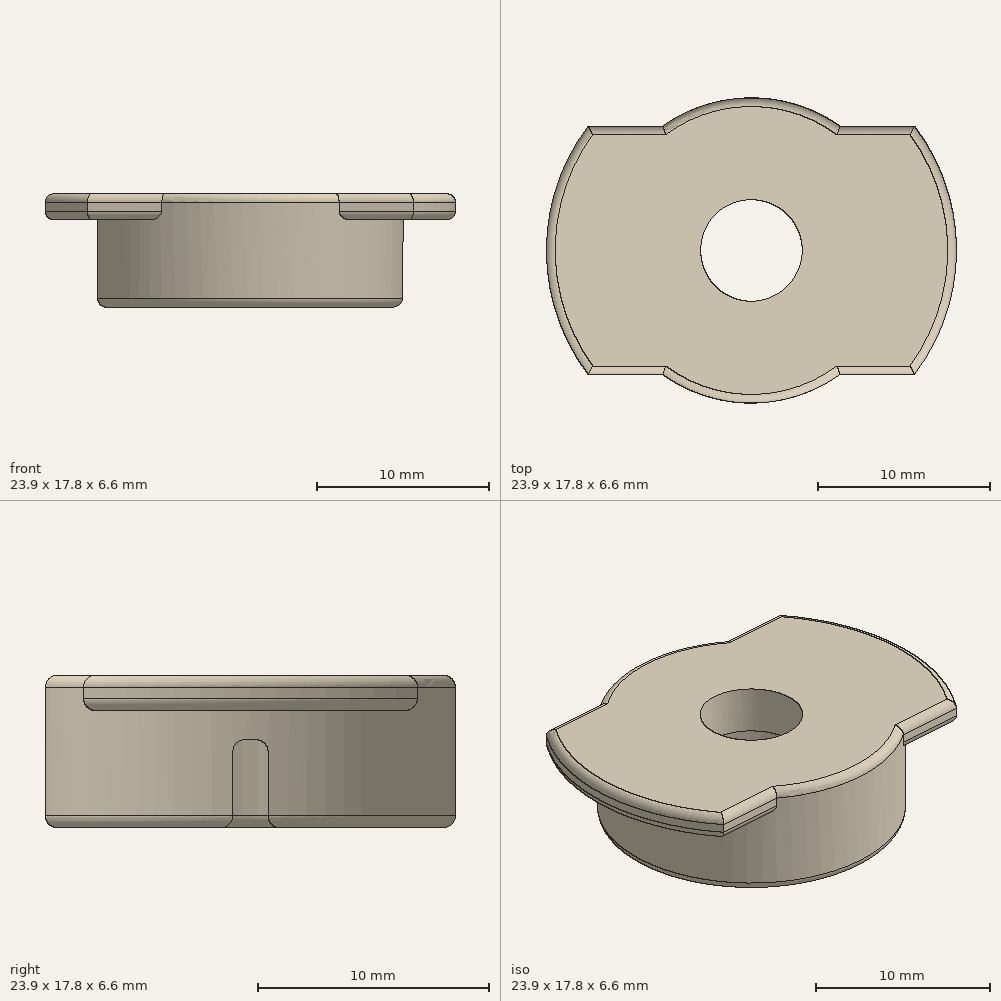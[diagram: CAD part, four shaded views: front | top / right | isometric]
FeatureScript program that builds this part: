
annotation { "Feature Type Name" : "Feature", "Feature Type Description" : "" }
export const myFeature = defineFeature(function(context is Context, id is Id, definition is map)
    precondition{}
    {
        {
            var Q0;
            Q0=qCreatedBy(makeId("Top.planeOp"),FACE);
            var sketch = newSketch(context, id + "F0", { "sketchPlane" : qUnion([Q0])});
            skCircle(sketch, "E0", {"center": v(0, 0) * mm, "radius": 11.94 * mm});
            skSolve(sketch);
        }
        {
            var Q0;
            Q0=makeQuery(id+"F0.imprint","IMPRINT",FACE,{"disambiguationData":[TD([[makeQuery(id+"F0.imprint","IMPRINT",EDGE,{"derivedFrom":sQuery(id+"F0.wireOp",EDGE,"E0")}),1.0]])]});
            var sketch = newSketch(context, id + "F1", { "sketchPlane" : qUnion([Q0])});
            skLineSegment(sketch, "E1", {"start": v(9.5, 7.24) * mm, "end": v(-9.5, 7.24) * mm});
            skLineSegment(sketch, "E2", {"start": v(9.5, -7.24) * mm, "end": v(-9.5, -7.24) * mm});
            skLineSegment(sketch, "E3", {"start": v(-9.5, 7.24) * mm, "end": v(-9.5, -7.24) * mm, "construction": true});
            skLineSegment(sketch, "E4", {"start": v(9.5, 7.24) * mm, "end": v(9.5, -7.24) * mm, "construction": true});
            skSolve(sketch);
        }
        {
            var Q0;
            Q0=qSketchRegion(id+"F0",true);
            extrude(context, id + "F2", {"entities" : qUnion([Q0]), "depth" : 1.52 * mm, "offsetDistance" : 25.4 * mm});
        }
        {
            var Q0;
            {var subQ0=sQuery(id+"F1.wireOp",EDGE,"E1");Q0=makeQuery(id+"F1.imprint","IMPRINT",FACE,{"disambiguationData":[TD([[makeQuery(id+"F1.imprint","IMPRINT",EDGE,{"derivedFrom":subQ0}),-1.0]])]});}
            var Q1;
            {var subQ0=sQuery(id+"F1.wireOp",EDGE,"E2");Q1=makeQuery(id+"F1.imprint","IMPRINT",FACE,{"disambiguationData":[TD([[makeQuery(id+"F1.imprint","IMPRINT",EDGE,{"derivedFrom":subQ0}),1.0]])]});}
            extrude(context, id + "F3", {"entities" : qUnion([Q0, Q1]), "operationType" : NewBodyOperationType.REMOVE, "depth" : 2.54 * mm, "offsetDistance" : 25.4 * mm, "hasSecondDirection" : true, "secondDirectionOppositeDirection" : true, "secondDirectionDepth" : 25.4 * mm});
        }
        {
            var Q0;
            Q0=makeQuery(id+"F2.opExtrude","CAP_FACE",FACE,{"disambiguationData":[OSD([sQuery(id+"F0.wireOp",EDGE,"E0")])],"isStart":true});
            var sketch = newSketch(context, id + "F4", { "sketchPlane" : qUnion([Q0])});
            skCircle(sketch, "E5", {"center": v(0, 0) * mm, "radius": 8.9 * mm});
            skSolve(sketch);
        }
        {
            var Q0;
            Q0=qSketchRegion(id+"F4",true);
            extrude(context, id + "F5", {"entities" : qUnion([Q0]), "operationType" : NewBodyOperationType.ADD, "oppositeDirection" : true, "depth" : 1.52 * mm, "offsetDistance" : 25.4 * mm});
        }
        {
            var Q0;
            Q0=makeQuery(id+"F5.boolean.opBoolean","MERGE",FACE,{"derivedFrom":[makeQuery(id+"F2.opExtrude","CAP_FACE",FACE,{"disambiguationData":[OSD([sQuery(id+"F0.wireOp",EDGE,"E0")])],"isStart":true}),makeQuery(id+"F5.opExtrude","CAP_FACE",FACE,{"disambiguationData":[OSD([sQuery(id+"F4.wireOp",EDGE,"E5")])],"isStart":true})]});
            var sketch = newSketch(context, id + "F6", { "sketchPlane" : qUnion([Q0])});
            skCircle(sketch, "E6", {"center": v(0, 0) * mm, "radius": 8.9 * mm});
            skSolve(sketch);
        }
        {
            var Q0;
            Q0=qSketchRegion(id+"F6",true);
            extrude(context, id + "F7", {"entities" : qUnion([Q0]), "operationType" : NewBodyOperationType.ADD, "depth" : 5.08 * mm, "offsetDistance" : 25.4 * mm});
        }
        {
            var Q0;
            Q0=makeQuery(id+"F7.opExtrude","CAP_FACE",FACE,{"disambiguationData":[OSD([sQuery(id+"F6.wireOp",EDGE,"E6")])],"isStart":false});
            var sketch = newSketch(context, id + "F8", { "sketchPlane" : qUnion([Q0])});
            skCircle(sketch, "E7", {"center": v(0, 0) * mm, "radius": 7.37 * mm});
            skSolve(sketch);
        }
        {
            var Q0;
            Q0 = qSketchRegion(id + "F8", true);
            extrude(context, id + "F9", {"entities" : qUnion([Q0]), "operationType" : NewBodyOperationType.REMOVE, "oppositeDirection" : true, "depth" : 5.08 * mm, "offsetDistance" : 25.4 * mm});
        }
        {
            var Q0;
            Q0=makeQuery(id+"F7.opExtrude","CAP_FACE",FACE,{"disambiguationData":[OSD([sQuery(id+"F6.wireOp",EDGE,"E6")])],"isStart":false});
            var sketch = newSketch(context, id + "F10", { "sketchPlane" : qUnion([Q0])});
            skLineSegment(sketch, "E8", {"start": v(8.86, -0.76) * mm, "end": v(7.33, -0.76) * mm});
            skLineSegment(sketch, "E9", {"start": v(8.86, 0.76) * mm, "end": v(7.33, 0.76) * mm});
            skLineSegment(sketch, "E10", {"start": v(0, 0) * mm, "end": v(8.9, 0) * mm, "construction": true});
            skArc(sketch, "E11", {"start": v(8.86, -0.76) * mm, "mid": v(8.9, 0) * mm, "end": v(8.86, 0.76) * mm});
            skArc(sketch, "E12", {"start": v(7.33, -0.76) * mm, "mid": v(7.37, 0) * mm, "end": v(7.33, 0.76) * mm});
            skSolve(sketch);
        }
        {
            var Q0;
            Q0=qCreatedBy(makeId("Front.planeOp"),FACE);
            var sketch = newSketch(context, id + "F11", { "sketchPlane" : qUnion([Q0])});
            skLineSegment(sketch, "E13", {"start": v(0, 0) * mm, "end": v(0, -7.62) * mm, "construction": true});
            skSolve(sketch);
        }
        {
            var Q0;
            Q0=makeQuery(id+"F10.imprint","IMPRINT",FACE,{"disambiguationData":[TD([[makeQuery(id+"F10.imprint","IMPRINT",EDGE,{"derivedFrom":sQuery(id+"F10.wireOp",EDGE,"E8")}),-1.0]])]});
            var Q1;
            Q1=makeQuery(id+"FOOJxRczT3KKHVt_1.3.F10.imprint","IMPRINT",FACE,{"disambiguationData":[TD([[makeQuery(id+"FOOJxRczT3KKHVt_1.3.F10.imprint","IMPRINT",EDGE,{"derivedFrom":sQuery(id+"FOOJxRczT3KKHVt_1.3.F10.wireOp",EDGE,"E8")}),-1.0]])]});
            var Q2;
            Q2=makeQuery(id+"FOOJxRczT3KKHVt_1.2.F10.imprint","IMPRINT",FACE,{"disambiguationData":[TD([[makeQuery(id+"FOOJxRczT3KKHVt_1.2.F10.imprint","IMPRINT",EDGE,{"derivedFrom":sQuery(id+"FOOJxRczT3KKHVt_1.2.F10.wireOp",EDGE,"E8")}),-1.0]])]});
            var Q3;
            Q3=makeQuery(id+"FOOJxRczT3KKHVt_1.1.F10.imprint","IMPRINT",FACE,{"disambiguationData":[TD([[makeQuery(id+"FOOJxRczT3KKHVt_1.1.F10.imprint","IMPRINT",EDGE,{"derivedFrom":sQuery(id+"FOOJxRczT3KKHVt_1.1.F10.wireOp",EDGE,"E8")}),-1.0]])]});
            extrude(context, id + "F12", {"entities" : qUnion([Q0, Q1, Q2, Q3]), "operationType" : NewBodyOperationType.REMOVE, "oppositeDirection" : true, "depth" : 3.8 * mm, "offsetDistance" : 25.4 * mm});
        }
        {
            var Q0;
            Q0=makeQuery(id+"F12.boolean.opBoolean","COPY",EDGE,{"derivedFrom":makeQuery(id+"F12.opExtrude","CAP_EDGE",EDGE,{"disambiguationData":[OSD([sQuery(id+"FOOJxRczT3KKHVt_1.2.F10.wireOp",EDGE,"E9")])],"isStart":false})});
            var Q1;
            Q1=makeQuery(id+"F12.boolean.opBoolean","COPY",EDGE,{"derivedFrom":makeQuery(id+"F12.opExtrude","CAP_EDGE",EDGE,{"disambiguationData":[OSD([sQuery(id+"FOOJxRczT3KKHVt_1.2.F10.wireOp",EDGE,"E8")])],"isStart":false})});
            var Q2;
            Q2=makeQuery(id+"F12.boolean.opBoolean","COPY",EDGE,{"derivedFrom":makeQuery(id+"F12.opExtrude","CAP_EDGE",EDGE,{"disambiguationData":[OSD([sQuery(id+"FOOJxRczT3KKHVt_1.1.F10.wireOp",EDGE,"E9")])],"isStart":false})});
            var Q3;
            Q3=makeQuery(id+"F12.boolean.opBoolean","COPY",EDGE,{"derivedFrom":makeQuery(id+"F12.opExtrude","CAP_EDGE",EDGE,{"disambiguationData":[OSD([sQuery(id+"FOOJxRczT3KKHVt_1.3.F10.wireOp",EDGE,"E8")])],"isStart":false})});
            var Q4;
            Q4=makeQuery(id+"F12.boolean.opBoolean","COPY",EDGE,{"derivedFrom":makeQuery(id+"F12.opExtrude","CAP_EDGE",EDGE,{"disambiguationData":[OSD([sQuery(id+"F10.wireOp",EDGE,"E9")])],"isStart":false})});
            var Q5;
            Q5=makeQuery(id+"F12.boolean.opBoolean","COPY",EDGE,{"derivedFrom":makeQuery(id+"F12.opExtrude","CAP_EDGE",EDGE,{"disambiguationData":[OSD([sQuery(id+"FOOJxRczT3KKHVt_1.3.F10.wireOp",EDGE,"E9")])],"isStart":false})});
            var Q6;
            Q6=makeQuery(id+"F12.boolean.opBoolean","COPY",EDGE,{"derivedFrom":makeQuery(id+"F12.opExtrude","CAP_EDGE",EDGE,{"disambiguationData":[OSD([sQuery(id+"F10.wireOp",EDGE,"E8")])],"isStart":false})});
            var Q7;
            Q7=makeQuery(id+"F12.boolean.opBoolean","COPY",EDGE,{"derivedFrom":makeQuery(id+"F12.opExtrude","CAP_EDGE",EDGE,{"disambiguationData":[OSD([sQuery(id+"FOOJxRczT3KKHVt_1.1.F10.wireOp",EDGE,"E8")])],"isStart":false})});
            fillet(context, id + "F13", {"entities" : qUnion([Q0, Q1, Q2, Q3, Q4, Q5, Q6, Q7]), "radius" : 0.5 * mm, "tangentPropagation" : true, "allowEdgeOverflow" : false});
        }
        {
            var Q0;
            Q0=makeQuery(id+"F12.boolean.opBoolean","COPY",EDGE,{"derivedFrom":makeQuery(id+"F12.opExtrude","SWEPT_EDGE",EDGE,{"disambiguationData":[OSD([sQuery(id+"F6.wireOp",EDGE,"E6"),sQuery(id+"F10.wireOp",EDGE,"E8"),sQuery(id+"F10.wireOp",EDGE,"E11")])]})});
            var Q1;
            Q1=makeQuery(id+"F12.boolean.opBoolean","COPY",EDGE,{"derivedFrom":makeQuery(id+"F12.opExtrude","SWEPT_EDGE",EDGE,{"disambiguationData":[OSD([sQuery(id+"F6.wireOp",EDGE,"E6"),sQuery(id+"F10.wireOp",EDGE,"E9"),sQuery(id+"F10.wireOp",EDGE,"E11")])]})});
            var Q2;
            Q2=makeQuery(id+"F12.boolean.opBoolean","COPY",EDGE,{"derivedFrom":makeQuery(id+"F12.opExtrude","SWEPT_EDGE",EDGE,{"disambiguationData":[OSD([sQuery(id+"F8.wireOp",EDGE,"E7"),sQuery(id+"F10.wireOp",EDGE,"E8"),sQuery(id+"F10.wireOp",EDGE,"E12")])]})});
            var Q3;
            Q3=makeQuery(id+"F12.boolean.opBoolean","COPY",EDGE,{"derivedFrom":makeQuery(id+"F12.opExtrude","SWEPT_EDGE",EDGE,{"disambiguationData":[OSD([sQuery(id+"F8.wireOp",EDGE,"E7"),sQuery(id+"F10.wireOp",EDGE,"E9"),sQuery(id+"F10.wireOp",EDGE,"E12")])]})});
            var Q4;
            {var subQ0=sQuery(id+"F6.wireOp",EDGE,"E6");Q4=makeQuery(id+"F12.boolean.opBoolean","SPLIT",EDGE,{"disambiguationData":[TD([makeQuery(id+"F12.opExtrude","SWEPT_FACE",FACE,{"disambiguationData":[OSD([sQuery(id+"F10.wireOp",EDGE,"E8")])]})])],"derivedFrom":makeQuery(id+"F7.opExtrude","CAP_EDGE",EDGE,{"disambiguationData":[OSD([subQ0])],"isStart":false})});}
            var Q5;
            {var subQ0=sQuery(id+"F8.wireOp",EDGE,"E7");Q5=makeQuery(id+"F12.boolean.opBoolean","SPLIT",EDGE,{"disambiguationData":[TD([makeQuery(id+"F12.opExtrude","SWEPT_FACE",FACE,{"disambiguationData":[OSD([sQuery(id+"F10.wireOp",EDGE,"E8")])]})])],"derivedFrom":makeQuery(id+"F9.boolean.opBoolean","COPY",EDGE,{"derivedFrom":makeQuery(id+"F9.opExtrude","CAP_EDGE",EDGE,{"disambiguationData":[OSD([subQ0])],"isStart":true})})});}
            var Q6;
            {var subQ0=sQuery(id+"F6.wireOp",EDGE,"E6");Q6=makeQuery(id+"F12.boolean.opBoolean","SPLIT",EDGE,{"disambiguationData":[TD([makeQuery(id+"F12.opExtrude","SWEPT_FACE",FACE,{"disambiguationData":[OSD([sQuery(id+"F10.wireOp",EDGE,"E9")])]})])],"derivedFrom":makeQuery(id+"F7.opExtrude","CAP_EDGE",EDGE,{"disambiguationData":[OSD([subQ0])],"isStart":false})});}
            var Q7;
            {var subQ0=sQuery(id+"F8.wireOp",EDGE,"E7");Q7=makeQuery(id+"F12.boolean.opBoolean","SPLIT",EDGE,{"disambiguationData":[TD([makeQuery(id+"F12.opExtrude","SWEPT_FACE",FACE,{"disambiguationData":[OSD([sQuery(id+"F10.wireOp",EDGE,"E9")])]})])],"derivedFrom":makeQuery(id+"F9.boolean.opBoolean","COPY",EDGE,{"derivedFrom":makeQuery(id+"F9.opExtrude","CAP_EDGE",EDGE,{"disambiguationData":[OSD([subQ0])],"isStart":true})})});}
            var Q8;
            Q8=makeQuery(id+"F12.boolean.opBoolean","COPY",EDGE,{"derivedFrom":makeQuery(id+"F12.opExtrude","CAP_EDGE",EDGE,{"disambiguationData":[OSD([sQuery(id+"F10.wireOp",EDGE,"E9")])],"isStart":true})});
            var Q9;
            Q9=makeQuery(id+"F12.boolean.opBoolean","COPY",EDGE,{"derivedFrom":makeQuery(id+"F12.opExtrude","CAP_EDGE",EDGE,{"disambiguationData":[OSD([sQuery(id+"F10.wireOp",EDGE,"E8")])],"isStart":true})});
            var Q10;
            {var subQ0=sQuery(id+"F6.wireOp",EDGE,"E6");Q10=makeQuery(id+"F12.boolean.opBoolean","SPLIT",EDGE,{"disambiguationData":[TD([makeQuery(id+"F12.opExtrude","SWEPT_FACE",FACE,{"disambiguationData":[OSD([sQuery(id+"FOOJxRczT3KKHVt_1.2.F10.wireOp",EDGE,"E9")])]})])],"derivedFrom":makeQuery(id+"F7.opExtrude","CAP_EDGE",EDGE,{"disambiguationData":[OSD([subQ0])],"isStart":false})});}
            var Q11;
            {var subQ0=sQuery(id+"F8.wireOp",EDGE,"E7");Q11=makeQuery(id+"F12.boolean.opBoolean","SPLIT",EDGE,{"disambiguationData":[TD([makeQuery(id+"F12.opExtrude","SWEPT_FACE",FACE,{"disambiguationData":[OSD([sQuery(id+"FOOJxRczT3KKHVt_1.2.F10.wireOp",EDGE,"E9")])]})])],"derivedFrom":makeQuery(id+"F9.boolean.opBoolean","COPY",EDGE,{"derivedFrom":makeQuery(id+"F9.opExtrude","CAP_EDGE",EDGE,{"disambiguationData":[OSD([subQ0])],"isStart":true})})});}
            var Q12;
            Q12=makeQuery(id+"F12.boolean.opBoolean","COPY",EDGE,{"derivedFrom":makeQuery(id+"F12.opExtrude","CAP_EDGE",EDGE,{"disambiguationData":[OSD([sQuery(id+"FOOJxRczT3KKHVt_1.3.F10.wireOp",EDGE,"E8")])],"isStart":true})});
            var Q13;
            Q13=makeQuery(id+"F12.boolean.opBoolean","COPY",EDGE,{"derivedFrom":makeQuery(id+"F12.opExtrude","CAP_EDGE",EDGE,{"disambiguationData":[OSD([sQuery(id+"FOOJxRczT3KKHVt_1.3.F10.wireOp",EDGE,"E9")])],"isStart":true})});
            var Q14;
            Q14=makeQuery(id+"F12.boolean.opBoolean","COPY",EDGE,{"derivedFrom":makeQuery(id+"F12.opExtrude","SWEPT_EDGE",EDGE,{"disambiguationData":[OSD([sQuery(id+"FOOJxRczT3KKHVt_1.3.F10.wireOp",EDGE,"E8"),sQuery(id+"FOOJxRczT3KKHVt_1.3.F10.wireOp",EDGE,"E11")])]})});
            var Q15;
            Q15=makeQuery(id+"F12.boolean.opBoolean","COPY",EDGE,{"derivedFrom":makeQuery(id+"F12.opExtrude","SWEPT_EDGE",EDGE,{"disambiguationData":[OSD([sQuery(id+"FOOJxRczT3KKHVt_1.3.F10.wireOp",EDGE,"E9"),sQuery(id+"FOOJxRczT3KKHVt_1.3.F10.wireOp",EDGE,"E11")])]})});
            var Q16;
            Q16=makeQuery(id+"F12.boolean.opBoolean","COPY",EDGE,{"derivedFrom":makeQuery(id+"F12.opExtrude","CAP_EDGE",EDGE,{"disambiguationData":[OSD([sQuery(id+"FOOJxRczT3KKHVt_1.1.F10.wireOp",EDGE,"E9")])],"isStart":true})});
            var Q17;
            Q17=makeQuery(id+"F12.boolean.opBoolean","COPY",EDGE,{"derivedFrom":makeQuery(id+"F12.opExtrude","CAP_EDGE",EDGE,{"disambiguationData":[OSD([sQuery(id+"FOOJxRczT3KKHVt_1.1.F10.wireOp",EDGE,"E8")])],"isStart":true})});
            var Q18;
            Q18=makeQuery(id+"F12.boolean.opBoolean","COPY",EDGE,{"derivedFrom":makeQuery(id+"F12.opExtrude","SWEPT_EDGE",EDGE,{"disambiguationData":[OSD([sQuery(id+"FOOJxRczT3KKHVt_1.1.F10.wireOp",EDGE,"E9"),sQuery(id+"FOOJxRczT3KKHVt_1.1.F10.wireOp",EDGE,"E11")])]})});
            var Q19;
            Q19=makeQuery(id+"F12.boolean.opBoolean","COPY",EDGE,{"derivedFrom":makeQuery(id+"F12.opExtrude","CAP_EDGE",EDGE,{"disambiguationData":[OSD([sQuery(id+"FOOJxRczT3KKHVt_1.2.F10.wireOp",EDGE,"E9")])],"isStart":true})});
            var Q20;
            Q20=makeQuery(id+"F12.boolean.opBoolean","COPY",EDGE,{"derivedFrom":makeQuery(id+"F12.opExtrude","CAP_EDGE",EDGE,{"disambiguationData":[OSD([sQuery(id+"FOOJxRczT3KKHVt_1.2.F10.wireOp",EDGE,"E8")])],"isStart":true})});
            var Q21;
            {var subQ0=sQuery(id+"F8.wireOp",EDGE,"E7");Q21=makeQuery(id+"F12.boolean.opBoolean","SPLIT",EDGE,{"disambiguationData":[TD([makeQuery(id+"F12.opExtrude","SWEPT_FACE",FACE,{"disambiguationData":[OSD([sQuery(id+"FOOJxRczT3KKHVt_1.1.F10.wireOp",EDGE,"E9")])]})])],"derivedFrom":makeQuery(id+"F9.boolean.opBoolean","COPY",EDGE,{"derivedFrom":makeQuery(id+"F9.opExtrude","CAP_EDGE",EDGE,{"disambiguationData":[OSD([subQ0])],"isStart":true})})});}
            var Q22;
            {var subQ0=sQuery(id+"F6.wireOp",EDGE,"E6");Q22=makeQuery(id+"F12.boolean.opBoolean","SPLIT",EDGE,{"disambiguationData":[TD([makeQuery(id+"F12.opExtrude","SWEPT_FACE",FACE,{"disambiguationData":[OSD([sQuery(id+"FOOJxRczT3KKHVt_1.1.F10.wireOp",EDGE,"E9")])]})])],"derivedFrom":makeQuery(id+"F7.opExtrude","CAP_EDGE",EDGE,{"disambiguationData":[OSD([subQ0])],"isStart":false})});}
            var Q23;
            {var subQ0=sQuery(id+"F6.wireOp",EDGE,"E6");Q23=makeQuery(id+"F12.boolean.opBoolean","SPLIT",FACE,{"disambiguationData":[TD([makeQuery(id+"F12.opExtrude","SWEPT_FACE",FACE,{"disambiguationData":[OSD([sQuery(id+"FOOJxRczT3KKHVt_1.1.F10.wireOp",EDGE,"E9")])]})])],"derivedFrom":makeQuery(id+"F7.opExtrude","CAP_FACE",FACE,{"disambiguationData":[OSD([subQ0])],"isStart":false})});}
            var Q24;
            Q24=makeQuery(id+"F12.boolean.opBoolean","COPY",EDGE,{"derivedFrom":makeQuery(id+"F12.opExtrude","SWEPT_EDGE",EDGE,{"disambiguationData":[OSD([sQuery(id+"FOOJxRczT3KKHVt_1.2.F10.wireOp",EDGE,"E8"),sQuery(id+"FOOJxRczT3KKHVt_1.2.F10.wireOp",EDGE,"E11")])]})});
            var Q25;
            Q25=makeQuery(id+"F12.boolean.opBoolean","COPY",EDGE,{"derivedFrom":makeQuery(id+"F12.opExtrude","SWEPT_EDGE",EDGE,{"disambiguationData":[OSD([sQuery(id+"FOOJxRczT3KKHVt_1.2.F10.wireOp",EDGE,"E9"),sQuery(id+"FOOJxRczT3KKHVt_1.2.F10.wireOp",EDGE,"E11")])]})});
            var Q26;
            Q26=makeQuery(id+"F12.boolean.opBoolean","COPY",EDGE,{"derivedFrom":makeQuery(id+"F12.opExtrude","SWEPT_EDGE",EDGE,{"disambiguationData":[OSD([sQuery(id+"FOOJxRczT3KKHVt_1.2.F10.wireOp",EDGE,"E9"),sQuery(id+"FOOJxRczT3KKHVt_1.2.F10.wireOp",EDGE,"E12")])]})});
            var Q27;
            Q27=makeQuery(id+"F12.boolean.opBoolean","COPY",EDGE,{"derivedFrom":makeQuery(id+"F12.opExtrude","SWEPT_EDGE",EDGE,{"disambiguationData":[OSD([sQuery(id+"FOOJxRczT3KKHVt_1.2.F10.wireOp",EDGE,"E8"),sQuery(id+"FOOJxRczT3KKHVt_1.2.F10.wireOp",EDGE,"E12")])]})});
            var Q28;
            Q28=makeQuery(id+"F12.boolean.opBoolean","COPY",EDGE,{"derivedFrom":makeQuery(id+"F12.opExtrude","SWEPT_EDGE",EDGE,{"disambiguationData":[OSD([sQuery(id+"FOOJxRczT3KKHVt_1.1.F10.wireOp",EDGE,"E9"),sQuery(id+"FOOJxRczT3KKHVt_1.1.F10.wireOp",EDGE,"E12")])]})});
            var Q29;
            Q29=makeQuery(id+"F12.boolean.opBoolean","COPY",EDGE,{"derivedFrom":makeQuery(id+"F12.opExtrude","SWEPT_EDGE",EDGE,{"disambiguationData":[OSD([sQuery(id+"FOOJxRczT3KKHVt_1.1.F10.wireOp",EDGE,"E8"),sQuery(id+"FOOJxRczT3KKHVt_1.1.F10.wireOp",EDGE,"E12")])]})});
            var Q30;
            Q30=makeQuery(id+"F12.boolean.opBoolean","COPY",EDGE,{"derivedFrom":makeQuery(id+"F12.opExtrude","SWEPT_EDGE",EDGE,{"disambiguationData":[OSD([sQuery(id+"FOOJxRczT3KKHVt_1.3.F10.wireOp",EDGE,"E8"),sQuery(id+"FOOJxRczT3KKHVt_1.3.F10.wireOp",EDGE,"E12")])]})});
            var Q31;
            Q31=makeQuery(id+"F12.boolean.opBoolean","COPY",EDGE,{"derivedFrom":makeQuery(id+"F12.opExtrude","SWEPT_EDGE",EDGE,{"disambiguationData":[OSD([sQuery(id+"FOOJxRczT3KKHVt_1.3.F10.wireOp",EDGE,"E9"),sQuery(id+"FOOJxRczT3KKHVt_1.3.F10.wireOp",EDGE,"E12")])]})});
            fillet(context, id + "F14", {"entities" : qUnion([Q0, Q1, Q2, Q3, Q4, Q5, Q6, Q7, Q8, Q9, Q10, Q11, Q12, Q13, Q14, Q15, Q16, Q17, Q18, Q19, Q20, Q21, Q22, Q23, Q24, Q25, Q26, Q27, Q28, Q29, Q30, Q31]), "radius" : 0.5 * mm, "tangentPropagation" : true, "allowEdgeOverflow" : false});
        }
        {
            var Q0;
            {var subQ0=sQuery(id+"F4.wireOp",EDGE,"E5");Q0=makeQuery(id+"F5.boolean.opBoolean","SPLIT",EDGE,{"disambiguationData":[TD([makeQuery(id+"F3.boolean.opBoolean","COPY",FACE,{"derivedFrom":makeQuery(id+"F3.opExtrude","SWEPT_FACE",FACE,{"disambiguationData":[OSD([sQuery(id+"F1.wireOp",EDGE,"E1")])]})})])],"derivedFrom":makeQuery(id+"F5.opExtrude","CAP_EDGE",EDGE,{"disambiguationData":[OSD([subQ0])],"isStart":false})});}
            var Q1;
            {var subQ0=sQuery(id+"F4.wireOp",EDGE,"E5");Q1=makeQuery(id+"F5.boolean.opBoolean","SPLIT",EDGE,{"disambiguationData":[TD([makeQuery(id+"F3.boolean.opBoolean","COPY",FACE,{"derivedFrom":makeQuery(id+"F3.opExtrude","SWEPT_FACE",FACE,{"disambiguationData":[OSD([sQuery(id+"F1.wireOp",EDGE,"E2")])]})})])],"derivedFrom":makeQuery(id+"F5.opExtrude","CAP_EDGE",EDGE,{"disambiguationData":[OSD([subQ0])],"isStart":false})});}
            var Q2;
            Q2=makeQuery(id+"F5.boolean.opBoolean","SPLIT",EDGE,{"disambiguationData":[OD(0.0)],"derivedFrom":makeQuery(id+"F3.boolean.opBoolean","INTERSECT",EDGE,{"derivedFrom":[makeQuery(id+"F2.opExtrude","CAP_FACE",FACE,{"disambiguationData":[OSD([sQuery(id+"F0.wireOp",EDGE,"E0")])],"isStart":false}),makeQuery(id+"F3.opExtrude","SWEPT_FACE",FACE,{"disambiguationData":[OSD([sQuery(id+"F1.wireOp",EDGE,"E2")])]})]})});
            var Q3;
            Q3=makeQuery(id+"F5.boolean.opBoolean","SPLIT",EDGE,{"disambiguationData":[OD(0.0)],"derivedFrom":makeQuery(id+"F3.boolean.opBoolean","INTERSECT",EDGE,{"derivedFrom":[makeQuery(id+"F2.opExtrude","CAP_FACE",FACE,{"disambiguationData":[OSD([sQuery(id+"F0.wireOp",EDGE,"E0")])],"isStart":false}),makeQuery(id+"F3.opExtrude","SWEPT_FACE",FACE,{"disambiguationData":[OSD([sQuery(id+"F1.wireOp",EDGE,"E1")])]})]})});
            var Q4;
            Q4=makeQuery(id+"F3.boolean.opBoolean","SPLIT",EDGE,{"disambiguationData":[OD(0.0)],"derivedFrom":makeQuery(id+"F2.opExtrude","CAP_EDGE",EDGE,{"disambiguationData":[OSD([sQuery(id+"F0.wireOp",EDGE,"E0")])],"isStart":false})});
            var Q5;
            Q5=makeQuery(id+"F5.boolean.opBoolean","SPLIT",EDGE,{"disambiguationData":[OD(1.0)],"derivedFrom":makeQuery(id+"F3.boolean.opBoolean","INTERSECT",EDGE,{"derivedFrom":[makeQuery(id+"F2.opExtrude","CAP_FACE",FACE,{"disambiguationData":[OSD([sQuery(id+"F0.wireOp",EDGE,"E0")])],"isStart":false}),makeQuery(id+"F3.opExtrude","SWEPT_FACE",FACE,{"disambiguationData":[OSD([sQuery(id+"F1.wireOp",EDGE,"E1")])]})]})});
            var Q6;
            Q6=makeQuery(id+"F3.boolean.opBoolean","SPLIT",EDGE,{"disambiguationData":[OD(1.0)],"derivedFrom":makeQuery(id+"F2.opExtrude","CAP_EDGE",EDGE,{"disambiguationData":[OSD([sQuery(id+"F0.wireOp",EDGE,"E0")])],"isStart":false})});
            var Q7;
            Q7=makeQuery(id+"F5.boolean.opBoolean","SPLIT",EDGE,{"disambiguationData":[OD(1.0)],"derivedFrom":makeQuery(id+"F3.boolean.opBoolean","INTERSECT",EDGE,{"derivedFrom":[makeQuery(id+"F2.opExtrude","CAP_FACE",FACE,{"disambiguationData":[OSD([sQuery(id+"F0.wireOp",EDGE,"E0")])],"isStart":false}),makeQuery(id+"F3.opExtrude","SWEPT_FACE",FACE,{"disambiguationData":[OSD([sQuery(id+"F1.wireOp",EDGE,"E2")])]})]})});
            var Q8;
            Q8=makeQuery(id+"F3.boolean.opBoolean","SPLIT",EDGE,{"disambiguationData":[OD(0.0)],"derivedFrom":makeQuery(id+"F2.opExtrude","CAP_EDGE",EDGE,{"disambiguationData":[OSD([sQuery(id+"F0.wireOp",EDGE,"E0")])],"isStart":true})});
            var Q9;
            Q9=makeQuery(id+"F3.boolean.opBoolean","SPLIT",EDGE,{"disambiguationData":[OD(1.0)],"derivedFrom":makeQuery(id+"F2.opExtrude","CAP_EDGE",EDGE,{"disambiguationData":[OSD([sQuery(id+"F0.wireOp",EDGE,"E0")])],"isStart":true})});
            var Q10;
            Q10=makeQuery(id+"F5.boolean.opBoolean","SPLIT",EDGE,{"disambiguationData":[OD(1.0)],"derivedFrom":makeQuery(id+"F3.boolean.opBoolean","INTERSECT",EDGE,{"derivedFrom":[makeQuery(id+"F2.opExtrude","CAP_FACE",FACE,{"disambiguationData":[OSD([sQuery(id+"F0.wireOp",EDGE,"E0")])],"isStart":true}),makeQuery(id+"F3.opExtrude","SWEPT_FACE",FACE,{"disambiguationData":[OSD([sQuery(id+"F1.wireOp",EDGE,"E2")])]})]})});
            var Q11;
            Q11=makeQuery(id+"F5.boolean.opBoolean","SPLIT",EDGE,{"disambiguationData":[OD(1.0)],"derivedFrom":makeQuery(id+"F3.boolean.opBoolean","INTERSECT",EDGE,{"derivedFrom":[makeQuery(id+"F2.opExtrude","CAP_FACE",FACE,{"disambiguationData":[OSD([sQuery(id+"F0.wireOp",EDGE,"E0")])],"isStart":true}),makeQuery(id+"F3.opExtrude","SWEPT_FACE",FACE,{"disambiguationData":[OSD([sQuery(id+"F1.wireOp",EDGE,"E1")])]})]})});
            var Q12;
            Q12=makeQuery(id+"F5.boolean.opBoolean","SPLIT",EDGE,{"disambiguationData":[OD(0.0)],"derivedFrom":makeQuery(id+"F3.boolean.opBoolean","INTERSECT",EDGE,{"derivedFrom":[makeQuery(id+"F2.opExtrude","CAP_FACE",FACE,{"disambiguationData":[OSD([sQuery(id+"F0.wireOp",EDGE,"E0")])],"isStart":true}),makeQuery(id+"F3.opExtrude","SWEPT_FACE",FACE,{"disambiguationData":[OSD([sQuery(id+"F1.wireOp",EDGE,"E1")])]})]})});
            var Q13;
            Q13=makeQuery(id+"F5.boolean.opBoolean","SPLIT",EDGE,{"disambiguationData":[OD(0.0)],"derivedFrom":makeQuery(id+"F3.boolean.opBoolean","INTERSECT",EDGE,{"derivedFrom":[makeQuery(id+"F2.opExtrude","CAP_FACE",FACE,{"disambiguationData":[OSD([sQuery(id+"F0.wireOp",EDGE,"E0")])],"isStart":true}),makeQuery(id+"F3.opExtrude","SWEPT_FACE",FACE,{"disambiguationData":[OSD([sQuery(id+"F1.wireOp",EDGE,"E2")])]})]})});
            fillet(context, id + "F15", {"entities" : qUnion([Q0, Q1, Q2, Q3, Q4, Q5, Q6, Q7, Q8, Q9, Q10, Q11, Q12, Q13]), "radius" : 0.5 * mm, "tangentPropagation" : true, "allowEdgeOverflow" : false});
        }
        {
            var Q0;
            Q0=makeQuery(id+"F9.boolean.opBoolean","COPY",FACE,{"derivedFrom":makeQuery(id+"F9.opExtrude","CAP_FACE",FACE,{"disambiguationData":[OSD([sQuery(id+"F8.wireOp",EDGE,"E7")])],"isStart":false})});
            var sketch = newSketch(context, id + "F16", { "sketchPlane" : qUnion([Q0])});
            skCircle(sketch, "E14", {"center": v(0, 0) * mm, "radius": 7.37 * mm});
            skSolve(sketch);
        }
        {
            var Q0;
            Q0 = qSketchRegion(id + "F16", true);
            extrude(context, id + "F17", {"entities" : qUnion([Q0]), "operationType" : NewBodyOperationType.ADD, "depth" : 1.27 * mm, "offsetDistance" : 25.4 * mm});
        }
        {
            var Q0;
            Q0=makeQuery(id+"F17.opExtrude","CAP_FACE",FACE,{"disambiguationData":[OSD([sQuery(id+"F16.wireOp",EDGE,"E14")])],"isStart":false});
            var sketch = newSketch(context, id + "F18", { "sketchPlane" : qUnion([Q0])});
            skCircle(sketch, "E15", {"center": v(0, 0) * mm, "radius": 2.96 * mm});
            skSolve(sketch);
        }
        {
            var Q0;
            Q0 = qSketchRegion(id + "F18", true);
            extrude(context, id + "F19", {"entities" : qUnion([Q0]), "operationType" : NewBodyOperationType.REMOVE, "oppositeDirection" : true, "depth" : 25.4 * mm, "offsetDistance" : 25.4 * mm, "hasSecondDirection" : true, "secondDirectionOppositeDirection" : false, "secondDirectionDepth" : 25.4 * mm});
        }
    });
